# Revit family: NAGARE_CURVED-OUTSIDE-45
name_source: partatom
category: Site
units: mm (PartAtom-declared; Revit-internal decimal feet)

## family parameters
Always vertical = Yes
Cut with Voids When Loaded = No
Part Type = Normal
Round Connector Dimension = Use Diameter
Shared = Yes
Work Plane-Based = Yes

## types (9) — shared parameters
Manufacturer = www.nagareconcrete.com
URL = https://www.nagareconcrete.com
materiaal_model = NAGARE_FME_(9-).f2_BETON_SI_BERSnl
offset_10 = 10 mm  [stored 0.0328084 ft]
voet_extra_hoogte = 850 mm  [stored 2.78871 ft]
zero-valued in all types: Default Elevation

## per-type parameters (varying)
| type | Type Comments | beugelpositie_hoogte | model_hoogte | oksel_maatvoering_breedte | oksel_maatvoering_hoogte | voet_hoogte | voet_lengte | zichtbaar_voet_type1 | zichtbaar_voet_type2 | zichtbaar_voet_type3 |
| C45LPO100/100 | C45LPO100/100 | 500 mm  [stored 1.64042 ft] | 1000 mm | 60 mm  [stored 0.19685 ft] | 60 mm  [stored 0.19685 ft] | 120 mm | 600 mm | Yes | No | No |
| C45LPO125/100 | C45LPO125/100 | 625 mm | 1250 mm | 90 mm | 90 mm | 120 mm | 850 mm  [stored 2.78871 ft] | Yes | No | No |
| C45LPO150/100 | C45LPO150/100 | 750 mm | 1500 mm | 90 mm | 90 mm | 120 mm | 850 mm  [stored 2.78871 ft] | Yes | No | No |
| C45LPO175/100 | C45LPO175/100 | 1350 mm | 1750 mm | 280 mm | 310 mm | 150 mm | 850 mm  [stored 2.78871 ft] | No | Yes | No |
| C45LPO200/100 | C45LPO200/100 | 750 mm | 2000 mm  [stored 6.56168 ft] | 280 mm | 310 mm | 150 mm | 850 mm  [stored 2.78871 ft] | No | Yes | No |
| C45LPO225/100 | C45LPO225/100 | 1350 mm | 2250 mm | 280 mm | 310 mm | 150 mm | 850 mm  [stored 2.78871 ft] | No | No | Yes |
| C45LPO250/100 | C45LPO250/100 | 1350 mm | 2500 mm | 280 mm | 310 mm | 150 mm | 850 mm  [stored 2.78871 ft] | No | No | Yes |
| C45LPO75/100 | C45LPO75/100 | 375 mm | 750 mm | 60 mm  [stored 0.19685 ft] | 60 mm  [stored 0.19685 ft] | 120 mm | 600 mm | Yes | No | No |
| C45LPO50/50 | C45LPO50/100 | 275 mm | 500 mm  [stored 1.64042 ft] | 60 mm  [stored 0.19685 ft] | 60 mm  [stored 0.19685 ft] | 120 mm | 600 mm | Yes | No | No |

note: [stored X ft] marks values corroborated as IEEE doubles in the binary element streams (Revit-internal decimal feet)

## geometry (parser evidence)
native form markers: Sweep x3
no freeform markers — native parametric forms only
